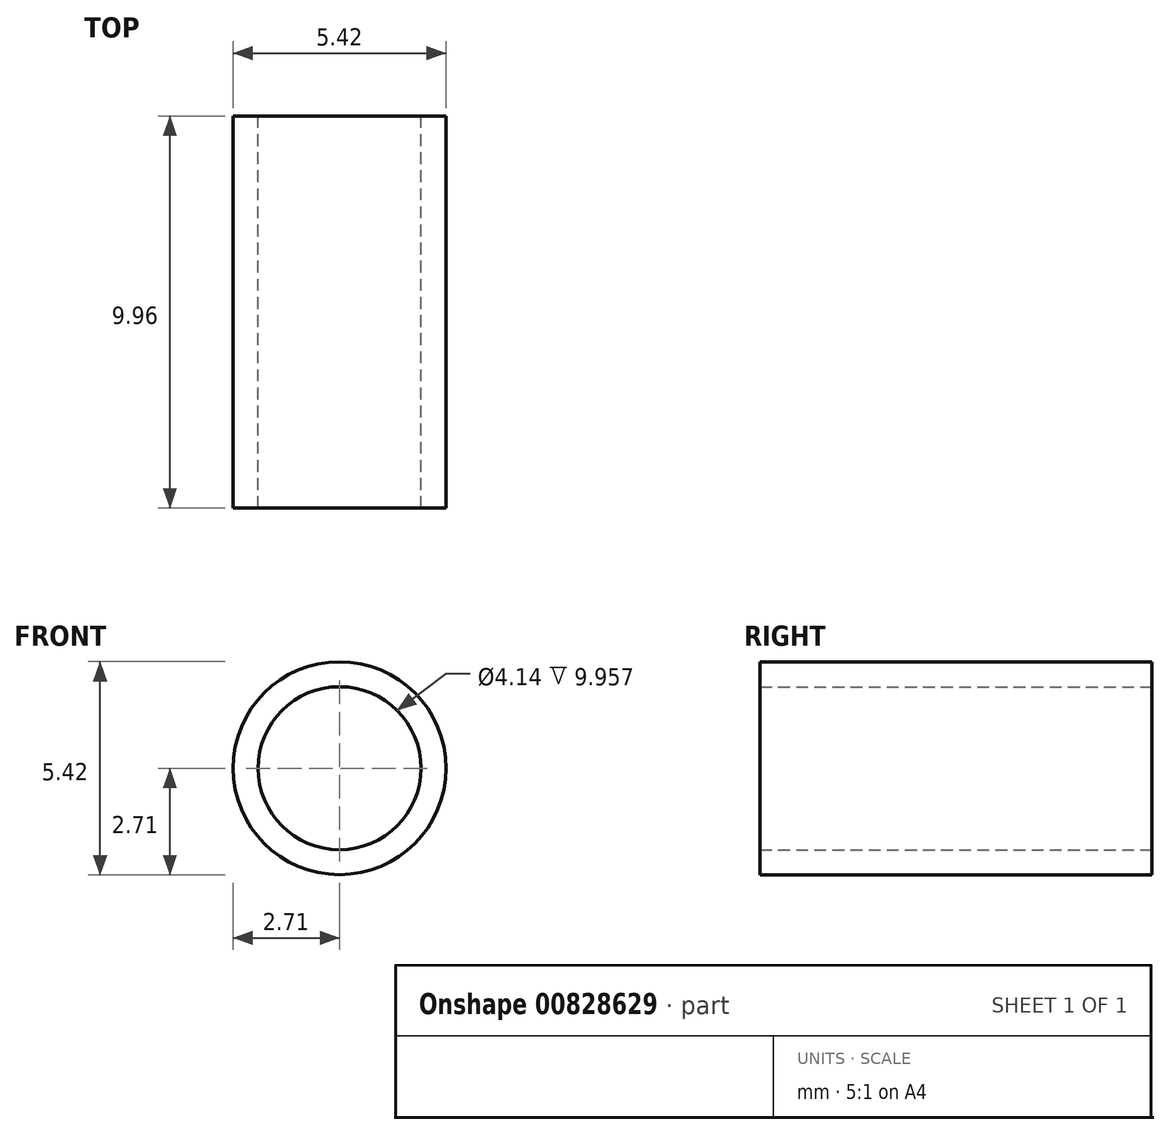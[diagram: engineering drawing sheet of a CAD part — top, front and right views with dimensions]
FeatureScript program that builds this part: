
annotation { "Feature Type Name" : "Feature", "Feature Type Description" : "" }
export const myFeature = defineFeature(function(context is Context, id is Id, definition is map)
    precondition{}
    {
        {
            var Q0;
            Q0=qCreatedBy(makeId("Front.planeOp"),FACE);
            var sketch = newSketch(context, id + "F0", { "sketchPlane" : qUnion([Q0])});
            skCircle(sketch, "E0", {"center": v(0, 0) * mm, "radius": 2.07 * mm});
            skCircle(sketch, "E1", {"center": v(0, 0) * mm, "radius": 2.7 * mm});
            skSolve(sketch);
        }
        {
            var Q0;
            Q0=makeQuery(id+"F0.imprint","IMPRINT",FACE,{"disambiguationData":[TD([[makeQuery(id+"F0.imprint","IMPRINT",EDGE,{"derivedFrom":sQuery(id+"F0.wireOp",EDGE,"E0")}),-1.0]])]});
            extrude(context, id + "F1", {"entities" : qUnion([Q0]), "endBound" : BoundingType.SYMMETRIC, "depth" : 9.96 * mm, "offsetDistance" : 25.4 * mm});
        }
    });
